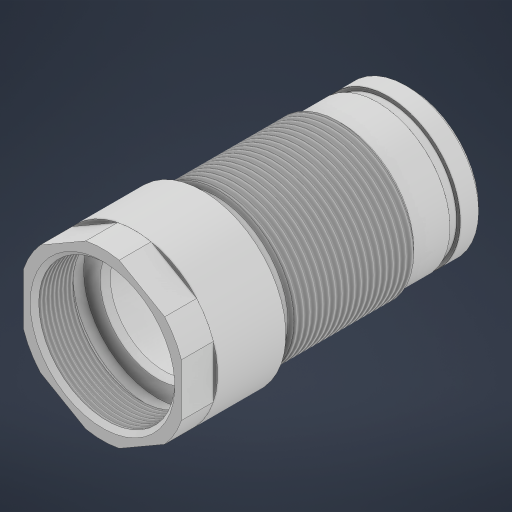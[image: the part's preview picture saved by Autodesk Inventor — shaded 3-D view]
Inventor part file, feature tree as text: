
AUTODESK INVENTOR PART (.ipt)
format: ipt  version: 2024.3 (Build 283343000, 343)  size: 373,760 bytes
history: native  units: mm
features: thread x2, sketch x2, revolve x1, extrude x1
ambient origin geometry x8: Origin, YZ Plane, XZ Plane, XY Plane, X Axis, Y Axis, Z Axis, Center Point
bodies: Solid1 (feature_tree)
feature tree (6):
  revolve  "Revolution1"  [1 undecoded]
  thread  "Thread1"  [1 undecoded]
  thread  "Thread2"  [1 undecoded]
  extrude  "Extrusion1"  TaperAngle=90.0deg  [1 undecoded]
  sketch  "Sketch1"  dims[d2=32.0mm d4=2.0mm d8=65.0mm d12=5.0mm]
  sketch  "Sketch2"  dims[d14=32.0mm d16=90.0deg d18=90.0deg d22=90.0deg d23=4.0mm d24=45.0deg d25=5.0mm d26=135.0deg d28=120.0deg d30=6.0mm d31=60.0deg d32=150.0deg d33=1.6mm d34=1.6mm d35=1.6mm d36=1.6mm d37=2.0mm d38=2.0mm d39=4.7mm d41=90.0deg d42=0.1mm d43=90.0deg d44=56.172mm d45=0.0mm d46=16.042mm d47=0.0mm d48=74.0mm d49=15.0mm d50=0.0mm]
note: 4 required parameter values undecoded (feature->parameter linkage not recoverable at this tier; creation-order binding heuristic only, values carry confidence <= 0.55)